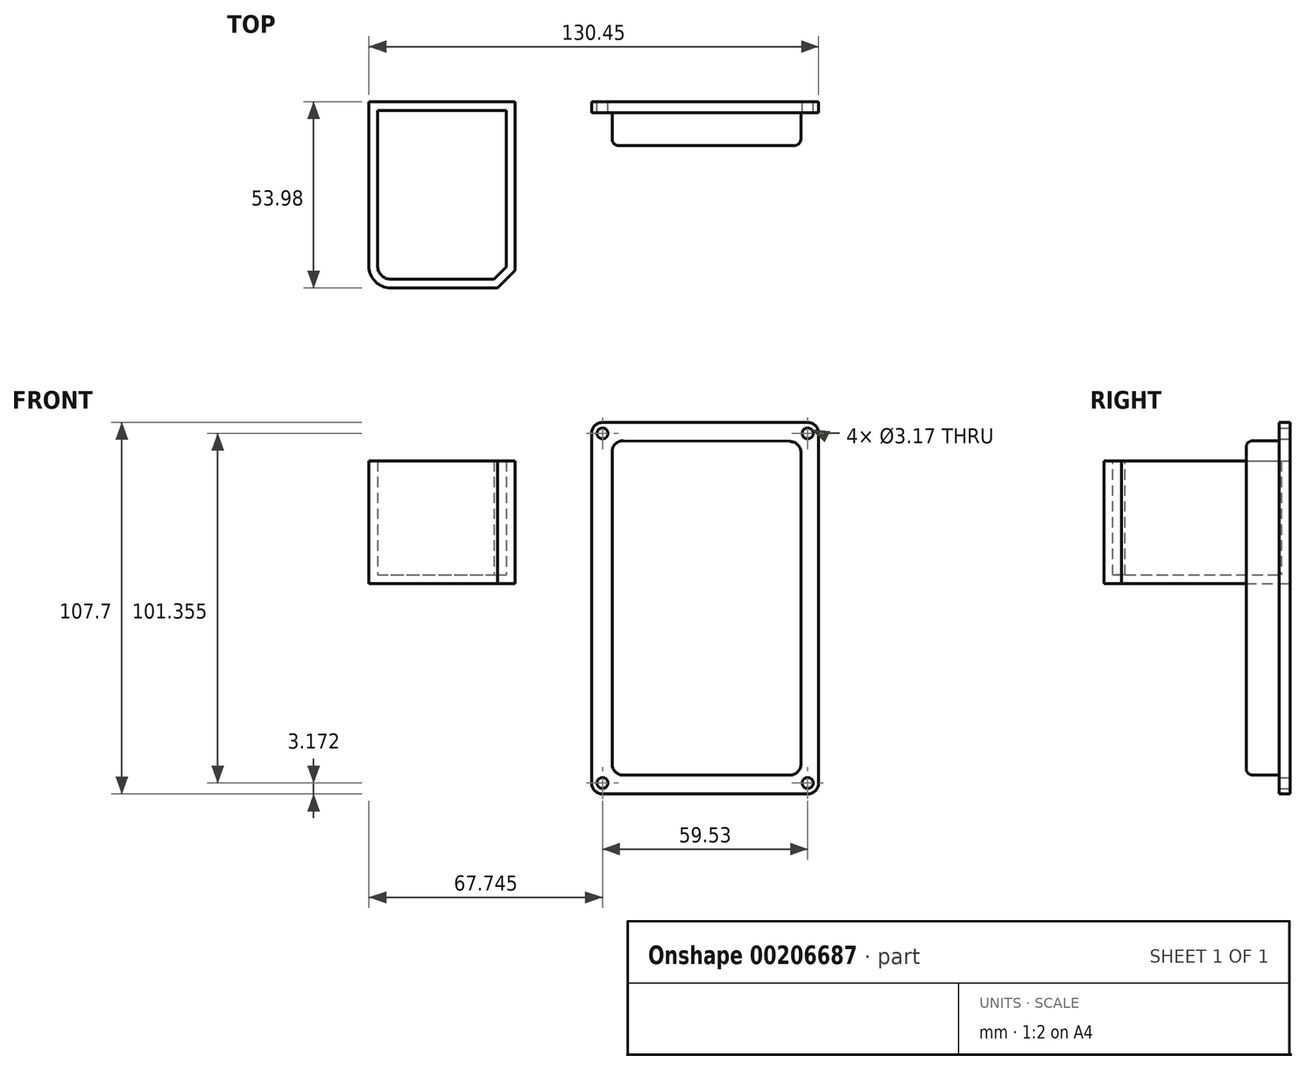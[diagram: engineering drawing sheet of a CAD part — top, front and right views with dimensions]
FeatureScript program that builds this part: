
annotation { "Feature Type Name" : "Feature", "Feature Type Description" : "" }
export const myFeature = defineFeature(function(context is Context, id is Id, definition is map)
    precondition{}
    {
        {
            var Q0;
            Q0=qCreatedBy(makeId("Front.planeOp"),FACE);
            var sketch = newSketch(context, id + "F0", { "sketchPlane" : qUnion([Q0])});
            skLineSegment(sketch, "E0.bottom", {"start": v(-29.76, 53.85) * mm, "end": v(29.76, 53.85) * mm});
            skLineSegment(sketch, "E0.top", {"start": v(-29.76, -53.85) * mm, "end": v(29.76, -53.85) * mm});
            skLineSegment(sketch, "E0.left", {"start": v(-32.94, 50.68) * mm, "end": v(-32.94, -50.68) * mm});
            skLineSegment(sketch, "E0.right", {"start": v(32.94, 50.68) * mm, "end": v(32.94, -50.68) * mm});
            skPoint(sketch, "E0.middle", {"position": v(0, 0) * mm});
            skPoint(sketch, "E1.visualSharp", {"position": v(-32.94, 53.85) * mm});
            skArc(sketch, "E1.filletArc", {"start": v(-29.76, 53.85) * mm, "mid": v(-32, 52.92) * mm, "end": v(-32.94, 50.68) * mm});
            skPoint(sketch, "E2.visualSharp", {"position": v(32.94, 53.85) * mm});
            skArc(sketch, "E2.filletArc", {"start": v(32.94, 50.68) * mm, "mid": v(32, 52.92) * mm, "end": v(29.76, 53.85) * mm});
            skPoint(sketch, "E3.visualSharp", {"position": v(32.94, -53.85) * mm});
            skArc(sketch, "E3.filletArc", {"start": v(29.76, -53.85) * mm, "mid": v(32, -52.92) * mm, "end": v(32.94, -50.68) * mm});
            skPoint(sketch, "E4.visualSharp", {"position": v(-32.94, -53.85) * mm});
            skArc(sketch, "E4.filletArc", {"start": v(-32.94, -50.68) * mm, "mid": v(-32, -52.92) * mm, "end": v(-29.76, -53.85) * mm});
            skLineSegment(sketch, "E5", {"start": v(-26.98, 45.37) * mm, "end": v(-26.98, -45.21) * mm});
            skLineSegment(sketch, "E6", {"start": v(-23.8, -48.39) * mm, "end": v(24.61, -48.39) * mm});
            skLineSegment(sketch, "E7", {"start": v(27.79, -45.21) * mm, "end": v(27.79, 45.17) * mm});
            skLineSegment(sketch, "E8", {"start": v(24.62, 48.34) * mm, "end": v(-23.79, 48.54) * mm});
            skPoint(sketch, "E9.visualSharp", {"position": v(-26.98, 48.55) * mm});
            skArc(sketch, "E9.filletArc", {"start": v(-23.79, 48.54) * mm, "mid": v(-26.04, 47.61) * mm, "end": v(-26.98, 45.37) * mm});
            skPoint(sketch, "E10.visualSharp", {"position": v(27.79, 48.33) * mm});
            skArc(sketch, "E10.filletArc", {"start": v(27.79, 45.17) * mm, "mid": v(26.86, 47.41) * mm, "end": v(24.62, 48.34) * mm});
            skPoint(sketch, "E11.visualSharp", {"position": v(27.79, -48.39) * mm});
            skArc(sketch, "E11.filletArc", {"start": v(24.61, -48.39) * mm, "mid": v(26.86, -47.46) * mm, "end": v(27.79, -45.21) * mm});
            skPoint(sketch, "E12.visualSharp", {"position": v(-26.98, -48.39) * mm});
            skArc(sketch, "E12.filletArc", {"start": v(-26.98, -45.21) * mm, "mid": v(-26.05, -47.46) * mm, "end": v(-23.8, -48.39) * mm});
            skPoint(sketch, "E13", {"position": v(-108.57, 36.06) * mm});
            skLineSegment(sketch, "E14.bottom", {"start": v(-97.51, 42.68) * mm, "end": v(-55.1, 42.68) * mm});
            skLineSegment(sketch, "E14.top", {"start": v(-97.51, 7.1) * mm, "end": v(-55.1, 7.1) * mm});
            skLineSegment(sketch, "E14.left", {"start": v(-97.51, 42.68) * mm, "end": v(-97.51, 7.1) * mm});
            skLineSegment(sketch, "E14.right", {"start": v(-55.1, 42.68) * mm, "end": v(-55.1, 7.1) * mm});
            skSolve(sketch);
        }
        {
            var Q0;
            Q0=makeQuery(id+"F0.imprint","IMPRINT",FACE,{"disambiguationData":[TD([[makeQuery(id+"F0.imprint","IMPRINT",EDGE,{"derivedFrom":sQuery(id+"F0.wireOp",EDGE,"E5")}),1.0]])]});
            extrude(context, id + "F1", {"entities" : qUnion([Q0]), "depth" : 12.7 * mm});
        }
        {
            var Q0;
            Q0 = qSketchRegion(id + "F0", true);
            extrude(context, id + "F2", {"entities" : qUnion([Q0]), "operationType" : NewBodyOperationType.ADD, "depth" : 3.17 * mm});
        }
        {
            var Q0;
            Q0=sQuery(id+"F0.wireOp",VERTEX,"E1.filletArc.center");
            var Q1;
            Q1=makeQuery(id+"F1.opExtrude","SWEPT_BODY",BODY,{"disambiguationData":[OSD([sQuery(id+"F0.wireOp",EDGE,"E5"),sQuery(id+"F0.wireOp",EDGE,"E6"),sQuery(id+"F0.wireOp",EDGE,"E7"),sQuery(id+"F0.wireOp",EDGE,"E8"),sQuery(id+"F0.wireOp",EDGE,"E9.filletArc"),sQuery(id+"F0.wireOp",EDGE,"E10.filletArc"),sQuery(id+"F0.wireOp",EDGE,"E11.filletArc"),sQuery(id+"F0.wireOp",EDGE,"E12.filletArc")])]});
            hole(context, id + "F3", {"style" : HoleStyle.SIMPLE, "endStyle" : HoleEndStyle.THROUGH, "oppositeDirection" : true, "holeDiameter" : 3.17 * mm, "locations" : qUnion([Q0]), "scope" : qUnion([Q1]), "isTappedThrough" : true});
        }
        {
            var Q0;
            Q0=sQuery(id+"F0.wireOp",VERTEX,"E2.filletArc.center");
            var Q1;
            Q1=sQuery(id+"F0.wireOp",VERTEX,"E4.filletArc.center");
            var Q2;
            Q2=sQuery(id+"F0.wireOp",VERTEX,"E3.filletArc.center");
            var Q3;
            Q3=makeQuery(id+"F1.opExtrude","SWEPT_BODY",BODY,{"disambiguationData":[OSD([sQuery(id+"F0.wireOp",EDGE,"E5"),sQuery(id+"F0.wireOp",EDGE,"E6"),sQuery(id+"F0.wireOp",EDGE,"E7"),sQuery(id+"F0.wireOp",EDGE,"E8"),sQuery(id+"F0.wireOp",EDGE,"E9.filletArc"),sQuery(id+"F0.wireOp",EDGE,"E10.filletArc"),sQuery(id+"F0.wireOp",EDGE,"E11.filletArc"),sQuery(id+"F0.wireOp",EDGE,"E12.filletArc")])]});
            hole(context, id + "F4", {"style" : HoleStyle.SIMPLE, "endStyle" : HoleEndStyle.THROUGH, "oppositeDirection" : true, "holeDiameter" : 3.17 * mm, "locations" : qUnion([Q0, Q1, Q2]), "scope" : qUnion([Q3]), "isTappedThrough" : true});
        }
        {
            var Q0;
            Q0=makeQuery(id+"F1.opExtrude","CAP_FACE",FACE,{"disambiguationData":[OSD([sQuery(id+"F0.wireOp",EDGE,"E5"),sQuery(id+"F0.wireOp",EDGE,"E6"),sQuery(id+"F0.wireOp",EDGE,"E7"),sQuery(id+"F0.wireOp",EDGE,"E8"),sQuery(id+"F0.wireOp",EDGE,"E9.filletArc"),sQuery(id+"F0.wireOp",EDGE,"E10.filletArc"),sQuery(id+"F0.wireOp",EDGE,"E11.filletArc"),sQuery(id+"F0.wireOp",EDGE,"E12.filletArc")])],"isStart":false});
            fillet(context, id + "F5", {"entities" : qUnion([Q0]), "radius" : 1.9 * mm, "tangentPropagation" : true, "allowEdgeOverflow" : false});
        }
        {
            var Q0;
            Q0=makeQuery(id+"F2.opExtrude","CAP_FACE",FACE,{"disambiguationData":[OSD([sQuery(id+"F0.wireOp",EDGE,"E14.bottom"),sQuery(id+"F0.wireOp",EDGE,"E14.top"),sQuery(id+"F0.wireOp",EDGE,"E14.left"),sQuery(id+"F0.wireOp",EDGE,"E14.right")])],"isStart":false});
            extrude(context, id + "F6", {"entities" : qUnion([Q0]), "operationType" : NewBodyOperationType.ADD, "depth" : 50.8 * mm});
        }
        {
            var Q0;
            Q0=makeQuery(id+"F6.opExtrude","CAP_EDGE",EDGE,{"disambiguationData":[OSD([sQuery(id+"F0.wireOp",EDGE,"E14.left")])],"isStart":false});
            fillet(context, id + "F7", {"entities" : qUnion([Q0]), "radius" : 6.35 * mm, "tangentPropagation" : true, "allowEdgeOverflow" : false});
        }
        {
            var Q0;
            Q0=makeQuery(id+"F6.opExtrude","CAP_EDGE",EDGE,{"disambiguationData":[OSD([sQuery(id+"F0.wireOp",EDGE,"E14.right")])],"isStart":false});
            chamfer(context, id + "F8", {"entities" : qUnion([Q0]), "width" : 5.08 * mm, "tangentPropagation" : true});
        }
        {
            var Q0;
            {var subQ0=sQuery(id+"F0.wireOp",EDGE,"E14.bottom");Q0=makeQuery(id+"F6.boolean.opBoolean","MERGE",FACE,{"derivedFrom":[makeQuery(id+"F2.opExtrude","SWEPT_FACE",FACE,{"disambiguationData":[OSD([subQ0])]}),makeQuery(id+"F6.opExtrude","SWEPT_FACE",FACE,{"disambiguationData":[OSD([subQ0])]})]});}
            shell(context, id + "F9", {"entities" : qUnion([Q0]), "thickness" : 2.54 * mm});
        }
    });
